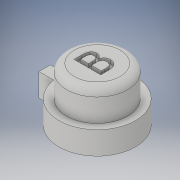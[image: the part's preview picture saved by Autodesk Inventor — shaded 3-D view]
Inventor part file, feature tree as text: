
AUTODESK INVENTOR PART (.ipt)
format: ipt  version: 2019 (Build 230136000, 136)  size: 185,344 bytes
history: native  units: mm
features: extrude x2, sketch x2, revolve x1
ambient origin geometry x8: Origin, YZ Plane, XZ Plane, XY Plane, X Axis, Y Axis, Z Axis, Center Point
bodies: Volumenkörper1 (feature_tree)
feature tree (5):
  revolve  "Umdrehung1"
  extrude  "Extrusion1"  Depth=4.0mm
  extrude  "Extrusion3"  Depth=5.0mm
  sketch  "Skizze2"  dims[d0=2.0mm d1=4.0mm]
  sketch  "Skizze4"  dims[d2=3.0mm d3=5.0mm d4=3.0mm d5=1.0mm d6=1.0mm d7=90.0deg d8=0.5mm d9=0.0mm d15=1.5mm d16=2.0mm d17=0.75mm d18=3.0mm d19=0.0mm]
